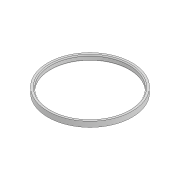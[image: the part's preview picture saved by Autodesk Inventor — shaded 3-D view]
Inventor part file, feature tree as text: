
AUTODESK INVENTOR PART (.ipt)
format: ipt  version: 2022 (Build 260153000, 153)  size: 108,544 bytes
history: native  units: mm
features: extrude x1, fillet x1, sketch x1
ambient origin geometry x8: Origin, YZ Plane, XZ Plane, XY Plane, X Axis, Y Axis, Z Axis, Center Point
bodies: Solid1 (feature_tree)
feature tree (3):
  extrude  "Extrusion1"  Depth=0.5mm
  fillet  "Fillet1"  Radius=2.7mm
  sketch  "Sketch1"  dims[d0=40.0mm d1=1.5mm d2=2.7mm d3=0.0mm d4=0.5mm]
